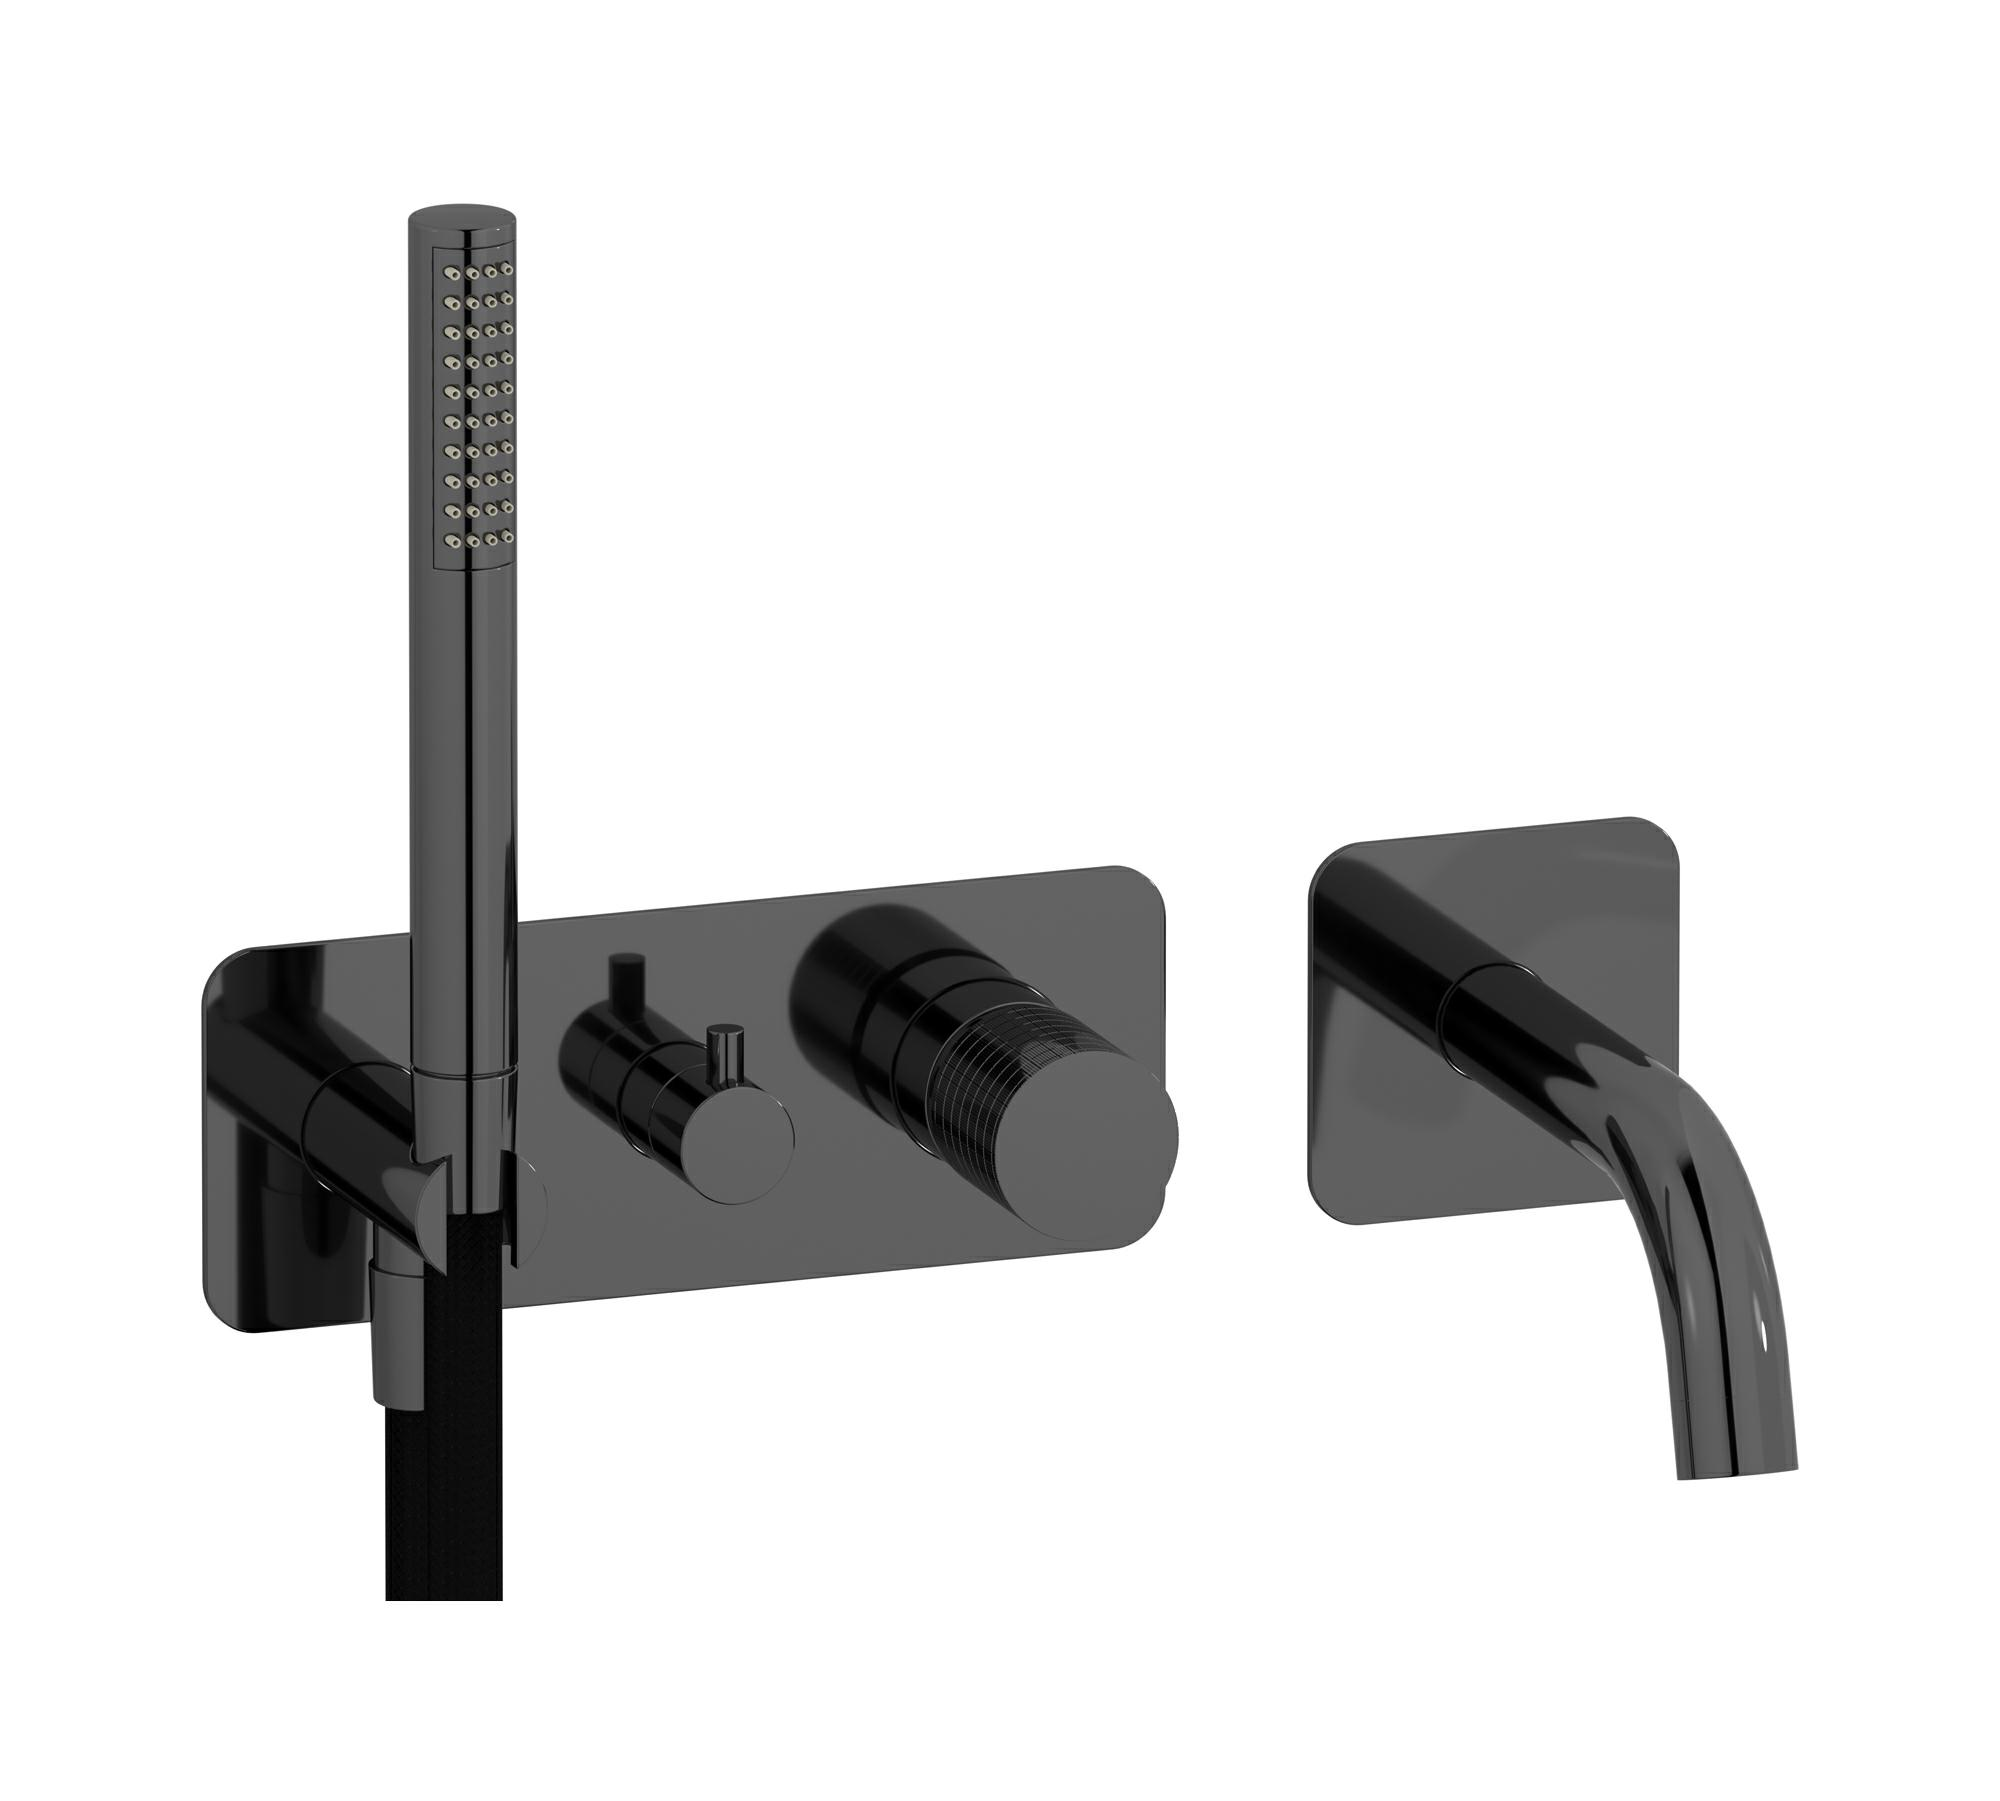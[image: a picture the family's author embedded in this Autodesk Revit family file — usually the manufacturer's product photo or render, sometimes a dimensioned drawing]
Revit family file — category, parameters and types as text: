
# Revit family: GA398
name_source: partatom
category: Apparecchi idraulici
units: mm (PartAtom-declared; Revit-internal decimal feet)

## family parameters
Basato su piano di lavoro = No
Condiviso = No
Mantieni orientamento annotazione = No
Numero OmniClass = 23.45.55.17
Punto di calcolo locali = No
Quota connettore circolare = Usa diametro
Sempre verticale = Sì
Taglio con vuoti quando caricato = No
Tipo di parte = Normale
Titolo OmniClass = Mixing Faucets

## types (12) — shared parameters
Cold water inlet = 10 mm  [stored 0.0328084 ft]
Commenti sul tipo = Wall mounted bath filler set with separate spout
Connessione CW = No
Connessione HW = No
Connessione di scarico = No
Connessione di ventilazione = No
Descrizione = Wall mounted bath filler set with separate spout
Hot water inlet = 10 mm  [stored 0.0328084 ft]
Produttore = IB Rubinetterie S.p.A.
URL = https://www.weareib.it
zero-valued in all types: Prospetto di default

## per-type parameters (varying)
| type | Finishes surface | Immagine tipo | Modello |
| Chrome | IB_Chrome | GA398CC.jpg | GA398CC |
| Black Chrome | IB_Black chrome | GA398CF.jpg | GA398CF |
| Brushed Black Chrome | IB_Brushed black chrome | GA398CS.jpg | GA398CS |
| Pale Gold | IB_Pale gold | GA398II.jpg | GA398II |
| Brushed Pale Gold | IB_brushed pale gold | GA398IS.jpg | GA398IS |
| Modern Bronze | IB_Modern bronze | GA398MB.jpg | GA398MB |
| Matt Black | IB_matt black | GA398NP.jpg | GA398NP |
| Gold | IB_gold | GA398OO.jpg | GA398OO |
| Brushed Gold | IB_brushed gold | GA398OS.jpg | GA398OS |
| Rose Gold | IB_Rose gold | GA398RS.jpg | GA398RS |
| Brushed Rose Gold | IB_Brushed rose gold | GA398SR.jpg | GA398SR |
| Brushed Nickel | IB_Brushed nickel | GA398SS.jpg | GA398SS |

note: [stored X ft] marks values corroborated as IEEE doubles in the binary element streams (Revit-internal decimal feet)
